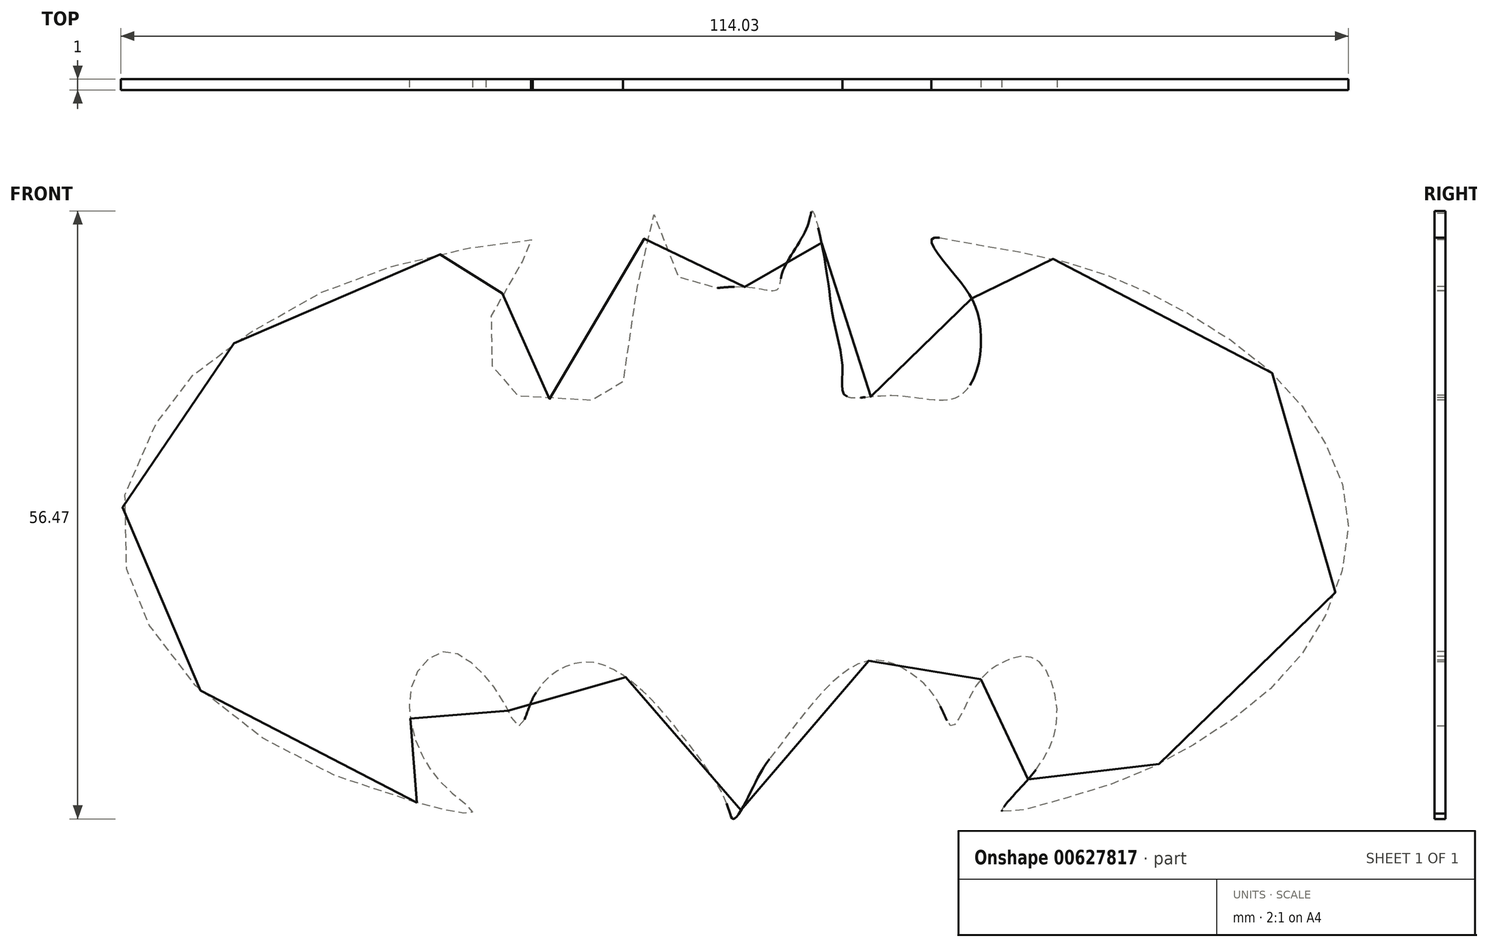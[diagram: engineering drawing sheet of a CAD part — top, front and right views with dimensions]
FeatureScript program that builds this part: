
annotation { "Feature Type Name" : "Feature", "Feature Type Description" : "" }
export const myFeature = defineFeature(function(context is Context, id is Id, definition is map)
    precondition{}
    {
        {
            var Q0;
            Q0=qCreatedBy(makeId("Front.planeOp"),FACE);
            var sketch = newSketch(context, id + "F0", { "sketchPlane" : qUnion([Q0])});
            skFitSpline(sketch, "E0", {"points": [v(-30.44, -25.8) * mm, v(-38.46, -23.1) * mm, v(-45.13, -19.55) * mm, v(-51.52, -14.37) * mm, v(-55.36, -9.18) * mm, v(-56.95, -5.56) * mm, v(-57.92, 0) * mm, v(-56.1, 6.82) * mm, v(-53.19, 11.56) * mm, v(-50.64, 14.47) * mm, v(-45.54, 18.12) * mm, v(-38.98, 21.76) * mm, v(-33.03, 23.95) * mm, v(-25.99, 25.65) * mm, v(-19.67, 26.62) * mm, v(-19.8, 26.5) * mm, v(-19.8, 26.62) * mm, v(-19.67, 25.65) * mm, v(-20.16, 25.04) * mm, v(-22.34, 21.76) * mm, v(-23.92, 18.12) * mm, v(-23.68, 15.32) * mm, v(-22.34, 13.02) * mm, v(-21.5, 12.17) * mm, v(-17.24, 11.68) * mm, v(-11.41, 11.92) * mm, v(-11.3, 12.53) * mm, v(-10.44, 18.48) * mm, v(-8.62, 28.92) * mm, v(-7.65, 26.98) * mm, v(-5.7, 22.12) * mm, v(-5.22, 21.76) * mm, v(0, 22.12) * mm, v(3.03, 21.88) * mm, v(3.52, 23.46) * mm, v(5.83, 27.7) * mm, v(6.31, 29.17) * mm, v(7.53, 24.19) * mm, v(8.26, 19.2) * mm, v(9.1, 14.47) * mm, v(9.35, 12.05) * mm, v(13.72, 12.05) * mm, v(19.55, 11.8) * mm, v(21.73, 14.96) * mm, v(21.61, 19.82) * mm, v(19.55, 23.22) * mm, v(17.36, 26.5) * mm, v(19.91, 26.37) * mm, v(27.8, 24.92) * mm, v(34.6, 22.85) * mm, v(41.77, 19.33) * mm, v(49.66, 13.5) * mm, v(54.4, 6.7) * mm, v(56.1, 0) * mm, v(54.16, -8) * mm, v(49.42, -14.67) * mm, v(42.38, -20.01) * mm, v(35.21, -23.65) * mm, v(27.32, -26.08) * mm, v(23.92, -26.69) * mm, v(26.1, -23.9) * mm, v(29.02, -18.07) * mm, v(27.08, -12.48) * mm, v(24.04, -12.73) * mm, v(21.37, -15.15) * mm, v(19.3, -18.68) * mm, v(18.1, -16.61) * mm, v(15.18, -13.58) * mm, v(11.53, -12.6) * mm, v(6.92, -15.88) * mm, v(2.91, -20.98) * mm, v(1.33, -23.29) * mm, v(-0.97, -27.3) * mm, v(-1.7, -25.72) * mm, v(-5.34, -20.13) * mm, v(-9.23, -15.64) * mm, v(-13.6, -12.85) * mm, v(-17, -13.33) * mm, v(-19.67, -16.13) * mm, v(-20.89, -18.68) * mm, v(-22.34, -16.5) * mm, v(-24.77, -13.33) * mm, v(-27.8, -11.75) * mm, v(-30.6, -14.06) * mm, v(-30.96, -18.43) * mm, v(-29.63, -21.95) * mm, v(-27.2, -24.87) * mm, v(-25.26, -26.69) * mm, v(-30.44, -25.8) * mm]});
            skSolve(sketch);
        }
        {
            var Q0;
            Q0=makeQuery(id+"F0.imprint","IMPRINT",FACE,{"disambiguationData":[TD([[makeQuery(id+"F0.imprint","IMPRINT",EDGE,{"derivedFrom":sQuery(id+"F0.wireOp",EDGE,"E0")}),-1.0]])]});
            extrude(context, id + "F1", {"entities" : qUnion([Q0]), "oppositeDirection" : true, "depth" : 1 * mm, "offsetDistance" : 25 * mm});
        }
    });
